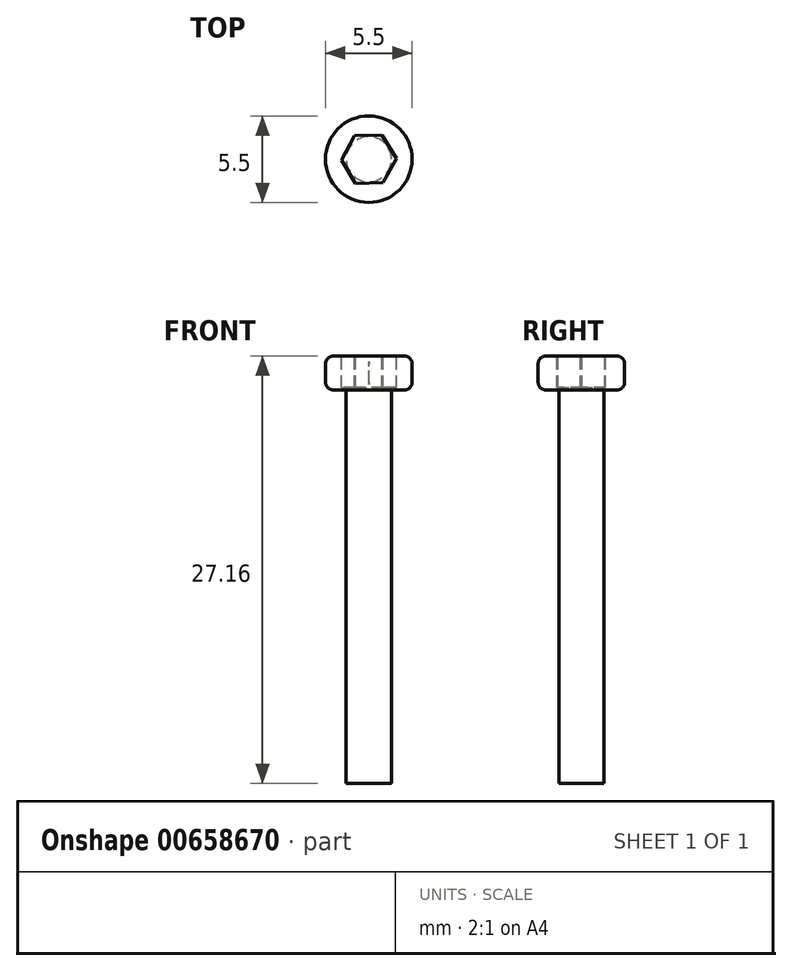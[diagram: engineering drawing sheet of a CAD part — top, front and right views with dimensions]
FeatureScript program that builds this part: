
annotation { "Feature Type Name" : "Feature", "Feature Type Description" : "" }
export const myFeature = defineFeature(function(context is Context, id is Id, definition is map)
    precondition{}
    {
        {
            var Q0;
            Q0=qCreatedBy(makeId("Front.planeOp"),FACE);
            var sketch = newSketch(context, id + "F0", { "sketchPlane" : qUnion([Q0])});
            skLineSegment(sketch, "E0", {"start": v(0, 0) * mm, "end": v(0, 2.16) * mm});
            skLineSegment(sketch, "E1", {"start": v(0, 2.16) * mm, "end": v(2.75, 2.16) * mm});
            skLineSegment(sketch, "E2", {"start": v(2.75, 2.16) * mm, "end": v(2.75, 0) * mm});
            skLineSegment(sketch, "E3", {"start": v(2.75, 0) * mm, "end": v(1.44, 0) * mm});
            skLineSegment(sketch, "E4", {"start": v(1.44, 0) * mm, "end": v(1.44, -25) * mm});
            skLineSegment(sketch, "E5", {"start": v(1.44, -25) * mm, "end": v(0, -25) * mm});
            skLineSegment(sketch, "E6", {"start": v(0, -25) * mm, "end": v(0, 0) * mm});
            skSolve(sketch);
        }
        {
            var Q0;
            Q0=makeQuery(id+"F0.imprint","IMPRINT",FACE,{"disambiguationData":[TD([[makeQuery(id+"F0.imprint","IMPRINT",EDGE,{"derivedFrom":sQuery(id+"F0.wireOp",EDGE,"E0")}),-1.0]])]});
            var Q1;
            Q1=sQuery(id+"F0.wireOp",EDGE,"E6");
            revolve(context, id + "F1", {"entities" : qUnion([Q0]), "axis" : qUnion([Q1]), "revolveType" : RevolveType.FULL});
        }
        {
            var Q0;
            Q0=makeQuery(id+"F1.opRevolve","SWEPT_EDGE",EDGE,{"disambiguationData":[OSD([sQuery(id+"F0.wireOp",EDGE,"E1"),sQuery(id+"F0.wireOp",EDGE,"E2")])]});
            var Q1;
            Q1=makeQuery(id+"F1.opRevolve","SWEPT_EDGE",EDGE,{"disambiguationData":[OSD([sQuery(id+"F0.wireOp",EDGE,"E2"),sQuery(id+"F0.wireOp",EDGE,"E3")])]});
            fillet(context, id + "F2", {"entities" : qUnion([Q0, Q1]), "radius" : .5 * mm, "tangentPropagation" : true, "allowEdgeOverflow" : false});
        }
        {
            var Q0;
            Q0=makeQuery(id+"F1.opRevolve","SWEPT_FACE",FACE,{"disambiguationData":[OSD([sQuery(id+"F0.wireOp",EDGE,"E1")])]});
            var sketch = newSketch(context, id + "F3", { "sketchPlane" : qUnion([Q0])});
            skCircle(sketch, "E7.cCircle", {"center": v(0, 0) * mm, "radius": 1.75 * mm, "construction": true});
            skLineSegment(sketch, "E7.0", {"start": v(0.84, 1.54) * mm, "end": v(1.75, 0.04) * mm});
            skLineSegment(sketch, "E7.1", {"start": v(1.75, 0.04) * mm, "end": v(0.91, -1.5) * mm});
            skLineSegment(sketch, "E7.2", {"start": v(0.91, -1.5) * mm, "end": v(-0.84, -1.54) * mm});
            skLineSegment(sketch, "E7.3", {"start": v(-0.84, -1.54) * mm, "end": v(-1.75, -0.04) * mm});
            skLineSegment(sketch, "E7.4", {"start": v(-1.75, -0.04) * mm, "end": v(-0.91, 1.5) * mm});
            skLineSegment(sketch, "E7.5", {"start": v(-0.91, 1.5) * mm, "end": v(0.84, 1.54) * mm});
            skSolve(sketch);
        }
        {
            var Q0;
            Q0=makeQuery(id+"F3.imprint","IMPRINT",FACE,{"disambiguationData":[TD([[makeQuery(id+"F3.imprint","IMPRINT",EDGE,{"derivedFrom":sQuery(id+"F3.wireOp",EDGE,"E7.0")}),-1.0]])]});
            extrude(context, id + "F4", {"entities" : qUnion([Q0]), "operationType" : NewBodyOperationType.REMOVE, "oppositeDirection" : true, "depth" : 2 * mm, "offsetDistance" : 25 * mm});
        }
        {
            var Q0;
            Q0=makeQuery(id+"F1.opRevolve","SWEPT_FACE",FACE,{"disambiguationData":[OSD([sQuery(id+"F0.wireOp",EDGE,"E1")])]});
            var sketch = newSketch(context, id + "F5", { "sketchPlane" : qUnion([Q0])});
            skCircle(sketch, "E8.0", {"center": v(0, 0) * mm, "radius": 2.75 * mm});
            skLineSegment(sketch, "E9", {"start": v(0, 2.75) * mm, "end": v(0, 2.72) * mm});
            skLineSegment(sketch, "E10", {"start": v(0, 2.72) * mm, "end": v(0.02, 2.75) * mm});
            skSolve(sketch);
        }
        {
            var Q0;
            {var subQ0=sQuery(id+"F5.wireOp",EDGE,"E9");Q0=makeQuery(id+"F5.imprint","IMPRINT",FACE,{"disambiguationData":[TD([[makeQuery(id+"F5.imprint","IMPRINT",EDGE,{"derivedFrom":subQ0}),1.0]])]});}
            extrude(context, id + "F6", {"entities" : qUnion([Q0]), "operationType" : NewBodyOperationType.REMOVE, "endBound" : BoundingType.THROUGH_ALL, "oppositeDirection" : true, "depth" : 25 * mm, "offsetDistance" : 25 * mm});
        }
    });
